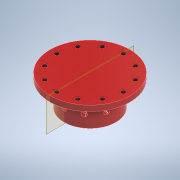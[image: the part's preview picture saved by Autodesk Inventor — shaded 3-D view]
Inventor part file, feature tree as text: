
AUTODESK INVENTOR PART (.ipt)
format: ipt  version: 2022.2 (Build 262287000, 287)  size: 233,984 bytes
history: native  units: mm
features: sketch x4, extrude x2, hole x2, plane x1, pattern_circular x1
ambient origin geometry x8: Origin, YZ Plane, XZ Plane, XY Plane, X Axis, Y Axis, Z Axis, Center Point
bodies: Body1 (feature_tree)
feature tree (10):
  extrude  "Extrusion26"  Depth=8.0mm
  hole  "Hole9"  [1 undecoded]
  extrude  "Extrusion29"  Depth=10.0mm TaperAngle=0.0deg
  plane  "Work Plane6"
  hole  "Hole10"  [1 undecoded]
  pattern_circular  "Circular Pattern1"  [2 undecoded]
  sketch  "Sketch51"  dims[d242=114.3mm d243=8.0mm]
  sketch  "Sketch58"  dims[d244=0.0mm d294=47.625mm]
  sketch  "Sketch59"  dims[d295=120.0mm d297=360.0deg]
  sketch  "Sketch60"  dims[d299=5.105mm d300=6.0mm d301=6.3754mm d302=9.525mm d303=14.3117mm d304=8.0mm d305=0.0mm d308=35.0mm d309=0.0mm d310=6.3754mm d311=6.0mm d312=6.985mm d313=5.76834mm d314=14.3117mm d315=10.0mm d316=0.0mm d317=100.0mm d318=360.0deg d321=58.039mm d322=8.0mm d64=1.0mm d65=1.0mm d66=1.0mm d67=0.15mm d68=0.25mm d69=0.375mm d70=14.3117mm d71=0.75mm d72=20.594885mm d73=0.0625mm d74=0.75mm d75=0.375mm]
note: 4 required parameter values undecoded (feature->parameter linkage not recoverable at this tier; creation-order binding heuristic only, values carry confidence <= 0.55)
